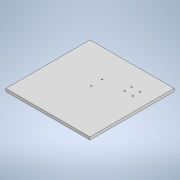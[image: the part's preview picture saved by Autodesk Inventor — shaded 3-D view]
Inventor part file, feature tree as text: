
AUTODESK INVENTOR PART (.ipt)
format: ipt  version: 2022 (Build 260153000, 153)  size: 115,200 bytes
history: native  units: mm
features: extrude x3, sketch x3
ambient origin geometry x8: Origin, YZ Plane, XZ Plane, XY Plane, X Axis, Y Axis, Z Axis, Center Point
bodies: Solid1 (feature_tree)
feature tree (6):
  extrude  "Extrusion1"  Depth=300.0mm
  extrude  "Extrusion2"  Depth=10.0mm
  extrude  "Extrusion3"  TaperAngle=0.0deg  [1 undecoded]
  sketch  "Sketch1"  dims[d0=300.0mm d1=300.0mm]
  sketch  "Sketch2"  dims[d2=10.0mm d3=0.0mm d4=50.0mm]
  sketch  "Sketch3"  dims[d7=4.2418mm d10=0.0mm d11=0.0mm d12=43.3mm d13=60.228mm d14=30.154mm d15=4.0mm d17=0.0mm d18=0.0mm]
note: 1 required parameter value undecoded (feature->parameter linkage not recoverable at this tier; creation-order binding heuristic only, values carry confidence <= 0.55)
